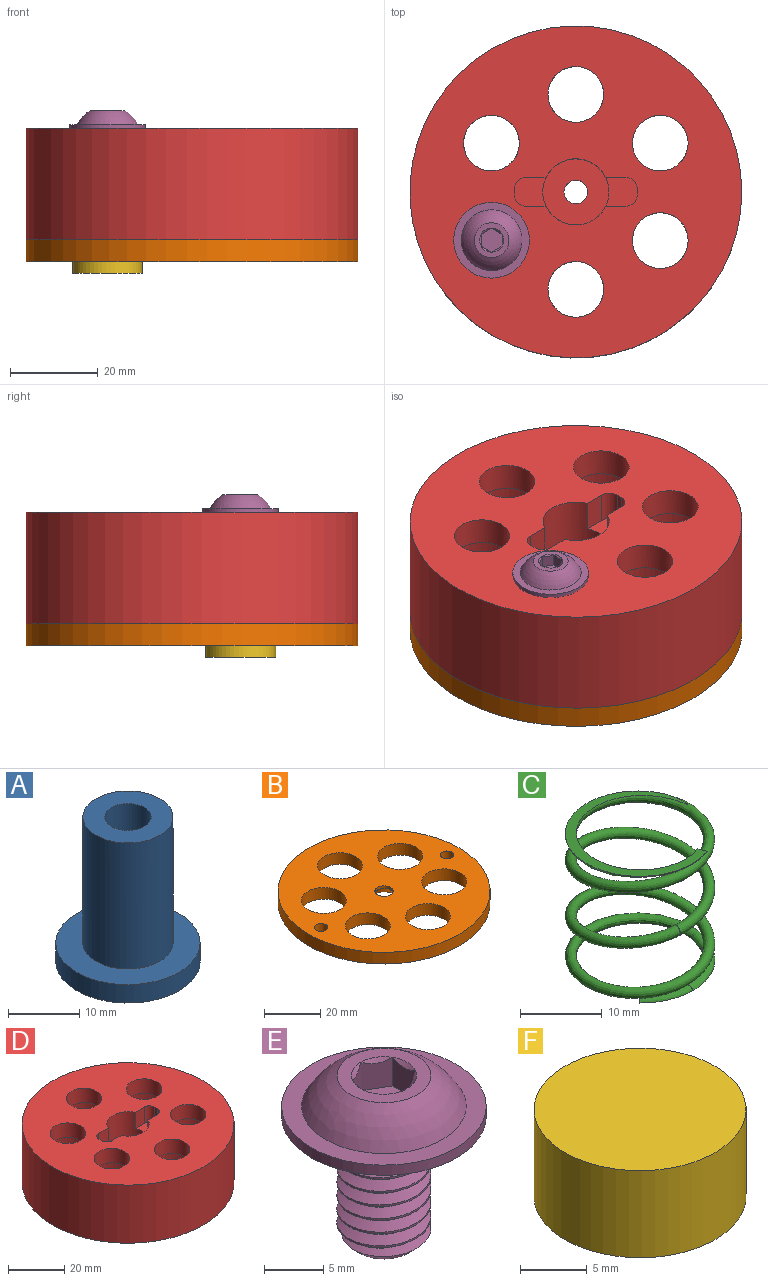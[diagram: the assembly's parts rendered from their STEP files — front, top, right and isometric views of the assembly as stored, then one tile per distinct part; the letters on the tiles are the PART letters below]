
ASSEMBLY  parts=6 mates=5
PART A: 20 faces, bbox 20.3x20.3x24.9 mm
  f0: cone r=2.75mm half-angle=45deg, axis (0,0,-1), area 1mm2, adj f8,f13
  f1: cone r=2.75mm half-angle=45deg, axis (0,0,-1), area 1mm2, adj f8,f14
  f2: cone r=2.75mm half-angle=45deg, axis (0,0,-1), area 1mm2, adj f8,f15
  f3: cone r=2.75mm half-angle=45deg, axis (0,0,-1), area 1mm2, adj f8,f16
  f4: cone r=2.75mm half-angle=45deg, axis (0,0,-1), area 1mm2, adj f8,f17
  f5: cone r=2.75mm half-angle=45deg, axis (0,0,-1), area 1mm2, adj f8,f18
  f6: cylinder r=10.16mm len=20.32mm, axis (0,0,-1), area 202.7mm2, adj f7,f8
  f7: plane 20.32x20.32mm, normal (0,0,1), area 197.6mm2, adj f6,f9
  f8: plane 20.32x20.32mm, normal (0,0,-1), area 300.5mm2, adj f0,f1,f2,f3,f4,f5,f6
  f9: cylinder r=6.35mm len=21.72mm, axis (0,0,-1), area 866.5mm2, adj f7,f10
  f10: plane 12.7x12.7mm, normal (0,0,1), area 93.2mm2, adj f9,f12
  f11: cone r=0mm half-angle=59deg, axis (0,0,1), area 39mm2, adj f12
  f12: cylinder r=3.26mm len=16.93mm, axis (0,0,1), area 347.3mm2, adj f10,f11
  f13: plane 3.81x2.38mm, normal (0.5,-0.87,0), area 9.8mm2, adj f0,f14,f18,f19
  f14: plane 3.81x2.38mm, normal (-0.5,-0.87,0), area 9.8mm2, adj f1,f13,f15,f19
  f15: plane 3.81x2.75mm, normal (-1,0,0), area 9.8mm2, adj f2,f14,f16,f19
  f16: plane 3.81x2.38mm, normal (-0.5,0.87,0), area 9.8mm2, adj f3,f15,f17,f19
  f17: plane 3.81x2.38mm, normal (0.5,0.87,0), area 9.8mm2, adj f4,f16,f18,f19
  f18: plane 3.81x2.75mm, normal (1,0,0), area 9.8mm2, adj f5,f13,f17,f19
  f19: plane 5.5x4.76mm, normal (0,0,-1), area 19.6mm2, adj f13,f14,f15,f16,f17,f18
PART B: 13 faces, bbox 75.7x75.7x5.1 mm
  f0: cylinder r=37.85mm len=75.69mm, axis (0,0,1), area 1208mm2, adj f1,f2
  f1: plane 75.69x75.69mm, normal (0,0,-1), area 3110.8mm2, adj f0,f3,f4,f5,f6,f7,f8,f9
  f2: plane 75.69x75.69mm, normal (0,0,1), area 3220.2mm2, adj f0,f3,f4,f5,f6,f7,f8,f9
  f3: cylinder r=2.38mm len=5.08mm, axis (0,0,-1), area 76mm2, adj f1,f2
  f4: cylinder r=2.38mm len=5.08mm, axis (0,0,-1), area 76mm2, adj f1,f2
  f5: cylinder r=8.01mm len=16.03mm, axis (0,0,-1), area 255.8mm2, adj f1,f2
  f6: cylinder r=8.01mm len=16.03mm, axis (0,0,-1), area 255.8mm2, adj f1,f2
  f7: cylinder r=8.01mm len=16.03mm, axis (0,0,-1), area 255.8mm2, adj f1,f2
  f8: cylinder r=8.01mm len=16.03mm, axis (0,0,-1), area 255.8mm2, adj f1,f2
  f9: cylinder r=8.01mm len=16.03mm, axis (0,0,-1), area 255.8mm2, adj f1,f2
  f10: cylinder r=8.01mm len=16.03mm, axis (0,0,-1), area 255.8mm2, adj f1,f2
  f11: cylinder r=3.26mm len=6.53mm, axis (0,0,-1), area 22.1mm2, adj f2,f12
  f12: cone r=3.26mm half-angle=41deg, axis (0,0,-1), area 166.8mm2, adj f1,f11
PART C: 8 faces, bbox 18.9x19.4x21 mm
  f0: bspline ~18.61x18.44mm, area 400mm2, adj f2,f3,f4
  f1: plane 0.93x0.93mm, normal (-0.71,0.71,0), area 0.3mm2, adj f2,f3
  f2: bspline ~6.46x3.66mm, area 11mm2, adj f0,f1,f3
  f3: plane 18.34x16.91mm, normal (0,0,-1), area 49.4mm2, adj f0,f1,f2
  f4: bspline ~18.69x18.58mm, area 400mm2, adj f0,f6,f7
  f5: plane 1.22x0.48mm, normal (0.94,0.34,0), area 0.3mm2, adj f6,f7
  f6: bspline ~6.99x2.87mm, area 11mm2, adj f4,f5,f7
  f7: plane 18.38x17.92mm, normal (0,0,1), area 52.6mm2, adj f4,f5,f6
PART D: 40 faces, bbox 75.7x75.7x25.4 mm
  f0: plane 75.69x75.69mm, normal (0,0,1), area 3479.4mm2, adj f2,f3,f6,f7,f9,f11,f12,f13
  f1: plane 75.69x75.69mm, normal (0,0,-1), area 2493.3mm2, adj f2,f5,f18,f21,f24,f27,f30,f33
  f2: cylinder r=37.85mm len=75.69mm, axis (0,0,1), area 6040mm2, adj f0,f1
  f3: cylinder r=7.54mm len=15.09mm, axis (0,0,1), area 530mm2, adj f0,f4,f6,f7,f8,f10,f11,f12
  f4: plane 15.09x15.09mm, normal (0,0,1), area 155.8mm2, adj f3,f5
  f5: cylinder r=2.71mm len=12.19mm, axis (0,0,-1), area 207.2mm2, adj f1,f4
  f6: plane 7.11x4.63mm, normal (0,-1,0), area 32.9mm2, adj f0,f3,f8,f16
  f7: plane 7.11x4.63mm, normal (0,1,0), area 32.9mm2, adj f0,f3,f8,f14
  f8: plane 7.17x6.53mm, normal (0,0,1), area 40.8mm2, adj f3,f6,f7,f9,f14,f16
  f9: plane 7.11x1.45mm, normal (1,0,0), area 10.3mm2, adj f0,f8,f14,f16
  f10: plane 7.17x6.53mm, normal (0,0,1), area 40.8mm2, adj f3,f11,f12,f13,f15,f17
  f11: plane 7.11x4.63mm, normal (0,1,0), area 32.9mm2, adj f0,f3,f10,f15
  f12: plane 7.11x4.63mm, normal (0,-1,0), area 32.9mm2, adj f0,f3,f10,f17
  f13: plane 7.11x1.45mm, normal (-1,0,0), area 10.3mm2, adj f0,f10,f15,f17
  f14: cylinder r=2.54mm len=7.11mm, axis (0,0,1), area 28.4mm2, adj f0,f7,f8,f9
  f15: cylinder r=2.54mm len=7.11mm, axis (0,0,-1), area 28.4mm2, adj f0,f10,f11,f13
  f16: cylinder r=2.54mm len=7.11mm, axis (0,0,-1), area 28.4mm2, adj f0,f6,f8,f9
  f17: cylinder r=2.54mm len=7.11mm, axis (0,0,1), area 28.4mm2, adj f0,f10,f12,f13
  f18: cylinder r=10.16mm len=20.32mm, axis (0,0,-1), area 1216.1mm2, adj f1,f19
  f19: plane 20.32x20.32mm, normal (0,0,-1), area 197.6mm2, adj f18,f20
  f20: cylinder r=6.35mm len=12.7mm, axis (0,0,-1), area 253.4mm2, adj f0,f19
  f21: cylinder r=10.16mm len=20.32mm, axis (0,0,-1), area 1216.1mm2, adj f1,f22
  f22: plane 20.32x20.32mm, normal (0,0,-1), area 197.6mm2, adj f21,f23
  f23: cylinder r=6.35mm len=12.7mm, axis (0,0,-1), area 253.4mm2, adj f0,f22
  f24: cylinder r=10.16mm len=20.32mm, axis (0,0,-1), area 1216.1mm2, adj f1,f25
  f25: plane 20.32x20.32mm, normal (0,0,-1), area 197.6mm2, adj f24,f26
  f26: cylinder r=6.35mm len=12.7mm, axis (0,0,-1), area 253.4mm2, adj f0,f25
  f27: cylinder r=10.16mm len=20.32mm, axis (0,0,-1), area 1216.1mm2, adj f1,f28
  f28: plane 20.32x20.32mm, normal (0,0,-1), area 197.6mm2, adj f27,f29
  f29: cylinder r=6.35mm len=12.7mm, axis (0,0,-1), area 253.4mm2, adj f0,f28
  f30: cylinder r=10.16mm len=20.32mm, axis (0,0,-1), area 1216.1mm2, adj f1,f31
  f31: plane 20.32x20.32mm, normal (0,0,-1), area 197.6mm2, adj f30,f32
  f32: cylinder r=6.35mm len=12.7mm, axis (0,0,-1), area 253.4mm2, adj f0,f31
  f33: cylinder r=10.16mm len=20.32mm, axis (0,0,-1), area 1216.1mm2, adj f1,f34
  f34: plane 20.32x20.32mm, normal (0,0,-1), area 197.6mm2, adj f33,f35
  f35: cylinder r=6.35mm len=12.7mm, axis (0,0,-1), area 253.4mm2, adj f0,f34
  f36: cylinder r=2.45mm len=6.35mm, axis (0,0,-1), area 97.8mm2, adj f1,f37
  f37: plane 4.9x4.9mm, normal (0,0,-1), area 18.9mm2, adj f36
  f38: cylinder r=2.45mm len=6.35mm, axis (0,0,-1), area 97.8mm2, adj f1,f39
  f39: plane 4.9x4.9mm, normal (0,0,-1), area 18.9mm2, adj f38
PART E: 25 faces, bbox 17.8x17.8x18 mm
  f0: cylinder r=3.97mm len=11.64mm, axis (0,0,-1), area 36.2mm2, adj f2,f4,f6,f7
  f1: cone r=2.91mm half-angle=45deg, axis (0,0,1), area 13.8mm2, adj f2,f3,f4,f5
  f2: cone r=2.91mm half-angle=45deg, axis (0,0,1), area 3.8mm2, adj f0,f1,f4,f6
  f3: plane 5.82x5.82mm, normal (0,0,-1), area 26.6mm2, adj f1
  f4: bspline ~13.93x7.94mm, area 199.7mm2, adj f0,f1,f2,f5,f7
  f5: cylinder r=3.05mm len=12.56mm, axis (0,0,-1), area 30.1mm2, adj f1,f4,f6,f7
  f6: bspline ~13.23x7.94mm, area 200.1mm2, adj f0,f2,f5,f7
  f7: plane 17.82x17.82mm, normal (0,0,-1), area 195.3mm2, adj f0,f4,f5,f6,f9
  f8: plane 17.27x17.27mm, normal (0,0,1), area 82.7mm2, adj f9,f11
  f9: cylinder r=8.64mm len=17.27mm, axis (0,0,-1), area 57.2mm2, adj f7,f8
  f10: plane 7.94x7.94mm, normal (0,0,1), area 25.7mm2, adj f11,f12,f13,f14,f15,f16,f17
  f11: sphere r=7.81mm, area 155.1mm2, adj f8,f10
  f12: cone r=2.75mm half-angle=45deg, axis (0,0,1), area 1mm2, adj f10,f19
  f13: cone r=2.75mm half-angle=45deg, axis (0,0,1), area 1mm2, adj f10,f20
  f14: cone r=2.75mm half-angle=45deg, axis (0,0,1), area 1mm2, adj f10,f21
  f15: cone r=2.75mm half-angle=45deg, axis (0,0,1), area 1mm2, adj f10,f22
  f16: cone r=2.75mm half-angle=45deg, axis (0,0,1), area 1mm2, adj f10,f23
  f17: cone r=2.75mm half-angle=45deg, axis (0,0,1), area 1mm2, adj f10,f24
  f18: plane 5.5x4.76mm, normal (0,0,1), area 19.6mm2, adj f19,f20,f21,f22,f23,f24
  f19: plane 2.95x2.75mm, normal (-1,0,0), area 7.4mm2, adj f12,f18,f20,f24
  f20: plane 2.95x2.38mm, normal (-0.5,-0.87,0), area 7.4mm2, adj f13,f18,f19,f21
  f21: plane 2.95x2.38mm, normal (0.5,-0.87,0), area 7.4mm2, adj f14,f18,f20,f22
  f22: plane 2.95x2.75mm, normal (1,0,0), area 7.5mm2, adj f15,f18,f21,f23
  f23: plane 2.95x2.38mm, normal (0.5,0.87,0), area 7.4mm2, adj f16,f18,f22,f24
  f24: plane 2.95x2.38mm, normal (-0.5,0.87,0), area 7.4mm2, adj f17,f18,f19,f23
PART F: 3 faces, bbox 15.9x15.9x8 mm
  f0: cylinder r=7.96mm len=15.93mm, axis (0,0,1), area 400.3mm2, adj f1,f2
  f1: plane 15.93x15.93mm, normal (0,0,-1), area 199.2mm2, adj f0
  f2: plane 15.93x15.93mm, normal (0,0,1), area 199.2mm2, adj f0
PLACE A t=(-19.25,11.11,0.32)mm
PLACE B at identity
PLACE C t=(19.25,11.11,9.3)mm
PLACE D at identity
PLACE E t=(-19.21,-11.03,29.43)mm
PLACE F t=(-19.25,-11.11,0.32)mm
MATE fastened F.f0 <-> A.f0  axis (0,0,1) through (-19.25,-11.11,0.32)mm
MATE fastened C.f3 <-> B.f7  axis (0,0,-1) through (19.25,11.11,0)mm
MATE slider A.f6 <-> D.f33  axis (0,0,-1) through (-19.25,-11.11,1.91)mm
MATE fastened D.f2 <-> B.f0  axis (0,0,-1) through (0,0,0)mm
MATE fastened E.f7 <-> A.f6  axis (0,0,-1) through (-19.25,-11.11,25.21)mm
